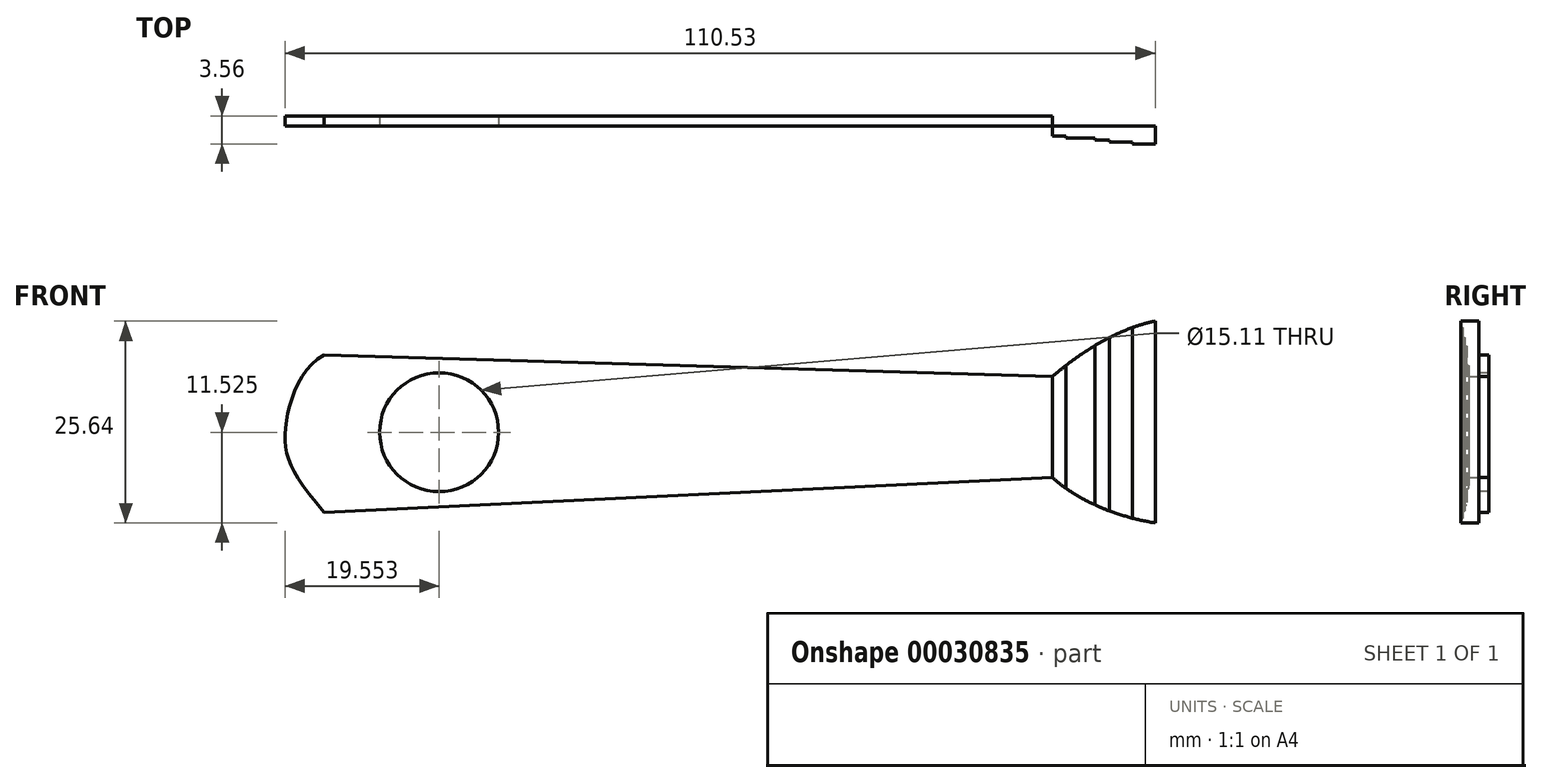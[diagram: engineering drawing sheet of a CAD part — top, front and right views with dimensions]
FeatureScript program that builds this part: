
annotation { "Feature Type Name" : "Feature", "Feature Type Description" : "" }
export const myFeature = defineFeature(function(context is Context, id is Id, definition is map)
    precondition{}
    {
        {
            var Q0;
            Q0=qCreatedBy(makeId("Front.planeOp"),FACE);
            var sketch = newSketch(context, id + "F0", { "sketchPlane" : qUnion([Q0])});
            skLineSegment(sketch, "E0", {"start": v(-63.78, 21.64) * mm, "end": v(28.7, 18.85) * mm});
            skLineSegment(sketch, "E1", {"start": v(28.7, 18.85) * mm, "end": v(28.7, 6.07) * mm});
            skLineSegment(sketch, "E2", {"start": v(28.7, 6.07) * mm, "end": v(-63.78, 1.64) * mm});
            skFitSpline(sketch, "E3", {"points": [v(-63.78, 21.64) * mm, v(-68.7, 12.13) * mm, v(-63.78, 1.64) * mm], "startDerivative": vector(-20.38, -11.32) * mm, "endDerivative": vector(25.28, -29.5) * mm});
            skFitSpline(sketch, "E4", {"points": [v(28.7, 18.85) * mm, v(44.43, 26.23) * mm, v(63.78, 18.85) * mm], "startDerivative": vector(26.79, 23.25) * mm, "endDerivative": vector(42.8, -21.58) * mm});
            skFitSpline(sketch, "E5", {"points": [v(28.7, 6.07) * mm, v(44.43, 0) * mm, v(63.78, 6.07) * mm], "startDerivative": vector(23.72, -21.65) * mm, "endDerivative": vector(41.38, 25.4) * mm});
            skLineSegment(sketch, "E6", {"start": v(63.78, 18.85) * mm, "end": v(44.43, 18.85) * mm});
            skLineSegment(sketch, "E7", {"start": v(63.78, 6.07) * mm, "end": v(44.43, 6.07) * mm});
            skLineSegment(sketch, "E8", {"start": v(44.43, 18.85) * mm, "end": v(63.78, 17.05) * mm});
            skLineSegment(sketch, "E9", {"start": v(63.78, 17.05) * mm, "end": v(44.43, 14.92) * mm});
            skLineSegment(sketch, "E10", {"start": v(44.43, 14.92) * mm, "end": v(63.78, 13.44) * mm});
            skLineSegment(sketch, "E11", {"start": v(63.78, 13.44) * mm, "end": v(44.43, 10.98) * mm});
            skLineSegment(sketch, "E12", {"start": v(44.43, 10.98) * mm, "end": v(63.61, 9.5) * mm});
            skLineSegment(sketch, "E13", {"start": v(63.61, 9.5) * mm, "end": v(44.43, 6.07) * mm});
            skCircle(sketch, "E14", {"center": v(-49.19, 11.8) * mm, "radius": 7.55 * mm});
            skLineSegment(sketch, "E15", {"start": v(44.43, 26.23) * mm, "end": v(44.43, 0) * mm});
            skLineSegment(sketch, "E16", {"start": v(35.97, 23.82) * mm, "end": v(35.97, 1.8) * mm});
            skLineSegment(sketch, "E17", {"start": v(54.1, 23.8) * mm, "end": v(54.1, 18.85) * mm});
            skLineSegment(sketch, "E18.trimOffspring", {"start": v(54.1, 6.07) * mm, "end": v(54.1, 1.35) * mm});
            skLineSegment(sketch, "E19.trimOffspring", {"start": v(54.1, 10.24) * mm, "end": v(54.1, 7.8) * mm});
            skLineSegment(sketch, "E20.trimOffspring", {"start": v(54.1, 14.18) * mm, "end": v(54.1, 12.21) * mm});
            skLineSegment(sketch, "E21.trimOffspring", {"start": v(54.1, 17.95) * mm, "end": v(54.1, 15.99) * mm});
            skLineSegment(sketch, "E22", {"start": v(30.47, 20.31) * mm, "end": v(30.47, 4.65) * mm});
            skLineSegment(sketch, "E23", {"start": v(38.9, 25.1) * mm, "end": v(38.9, 0.88) * mm});
            skLineSegment(sketch, "E24", {"start": v(41.8, 0.28) * mm, "end": v(41.8, 25.92) * mm});
            skLineSegment(sketch, "E25", {"start": v(34.1, 22.79) * mm, "end": v(34.1, 2.59) * mm});
            skLineSegment(sketch, "E26", {"start": v(49.69, 25.5) * mm, "end": v(49.36, 0.2) * mm});
            skLineSegment(sketch, "E27", {"start": v(57.88, 21.93) * mm, "end": v(57.88, 18.85) * mm});
            skLineSegment(sketch, "E28", {"start": v(60.58, 20.5) * mm, "end": v(60.58, 18.85) * mm});
            skLineSegment(sketch, "E29", {"start": v(52, 24.7) * mm, "end": v(52, 18.85) * mm});
            skLineSegment(sketch, "E30", {"start": v(47.3, 0) * mm, "end": v(47.3, 26.04) * mm});
            skLineSegment(sketch, "E31.trimOffspring", {"start": v(60.58, 6.07) * mm, "end": v(60.58, 4.22) * mm});
            skLineSegment(sketch, "E32.trimOffspring", {"start": v(57.88, 6.07) * mm, "end": v(57.88, 2.86) * mm});
            skLineSegment(sketch, "E33.trimOffspring", {"start": v(60.58, 9.74) * mm, "end": v(60.58, 8.97) * mm});
            skLineSegment(sketch, "E34.trimOffspring", {"start": v(57.88, 9.95) * mm, "end": v(57.88, 8.48) * mm});
            skLineSegment(sketch, "E35.trimOffspring", {"start": v(57.88, 13.9) * mm, "end": v(57.88, 12.7) * mm});
            skLineSegment(sketch, "E36.trimOffspring", {"start": v(60.58, 13.69) * mm, "end": v(60.58, 13.04) * mm});
            skLineSegment(sketch, "E37.trimOffspring", {"start": v(52, 6.07) * mm, "end": v(52, 0.73) * mm});
            skLineSegment(sketch, "E38.trimOffspring", {"start": v(52, 10.4) * mm, "end": v(52, 7.42) * mm});
            skLineSegment(sketch, "E39.trimOffspring", {"start": v(52, 14.34) * mm, "end": v(52, 11.95) * mm});
            skLineSegment(sketch, "E40.trimOffspring", {"start": v(57.88, 17.6) * mm, "end": v(57.88, 16.4) * mm});
            skLineSegment(sketch, "E41.trimOffspring", {"start": v(60.58, 17.35) * mm, "end": v(60.58, 16.7) * mm});
            skLineSegment(sketch, "E42.trimOffspring", {"start": v(52, 18.15) * mm, "end": v(52, 15.75) * mm});
            skSolve(sketch);
        }
        {
            var Q0;
            Q0=makeQuery(id+"F0.imprint","IMPRINT",FACE,{"disambiguationData":[TD([[makeQuery(id+"F0.imprint","IMPRINT",EDGE,{"derivedFrom":sQuery(id+"F0.wireOp",EDGE,"E0")}),-1.0]])]});
            extrude(context, id + "F1", {"entities" : qUnion([Q0]), "oppositeDirection" : true, "depth" : 1.27 * mm});
        }
        {
            var Q0;
            Q0=makeQuery(id+"F0.imprint","IMPRINT",FACE,{"disambiguationData":[TD([[makeQuery(id+"F0.imprint","IMPRINT",EDGE,{"derivedFrom":sQuery(id+"F0.wireOp",EDGE,"E1")}),1.0]])]});
            extrude(context, id + "F2", {"entities" : qUnion([Q0]), "operationType" : NewBodyOperationType.ADD, "depth" : 1.27 * mm});
        }
        {
            var Q0;
            {var subQ2=sQuery(id+"F0.wireOp",EDGE,"E22");Q0=makeQuery(id+"F0.imprint","IMPRINT",FACE,{"disambiguationData":[TD([[makeQuery(id+"F0.imprint","IMPRINT",EDGE,{"derivedFrom":subQ2}),1.0]])]});}
            extrude(context, id + "F3", {"entities" : qUnion([Q0]), "operationType" : NewBodyOperationType.ADD, "depth" : 1.52 * mm});
        }
        {
            var Q0;
            {var subQ1=sQuery(id+"F0.wireOp",EDGE,"E16");Q0=makeQuery(id+"F0.imprint","IMPRINT",FACE,{"disambiguationData":[TD([[makeQuery(id+"F0.imprint","IMPRINT",EDGE,{"derivedFrom":subQ1}),-1.0]])]});}
            extrude(context, id + "F5", {"entities" : qUnion([Q0]), "operationType" : NewBodyOperationType.ADD, "depth" : 1.78 * mm});
        }
        {
            var Q0;
            {var subQ1=sQuery(id+"F0.wireOp",EDGE,"E16");Q0=makeQuery(id+"F0.imprint","IMPRINT",FACE,{"disambiguationData":[TD([[makeQuery(id+"F0.imprint","IMPRINT",EDGE,{"derivedFrom":subQ1}),1.0]])]});}
            extrude(context, id + "F4", {"entities" : qUnion([Q0]), "operationType" : NewBodyOperationType.ADD, "depth" : 2.03 * mm});
        }
        {
            var Q0;
            {var subQ1=sQuery(id+"F0.wireOp",EDGE,"E23");Q0=makeQuery(id+"F0.imprint","IMPRINT",FACE,{"disambiguationData":[TD([[makeQuery(id+"F0.imprint","IMPRINT",EDGE,{"derivedFrom":subQ1}),1.0]])]});}
            extrude(context, id + "F6", {"entities" : qUnion([Q0]), "operationType" : NewBodyOperationType.ADD, "depth" : 2.3 * mm});
        }
    });
